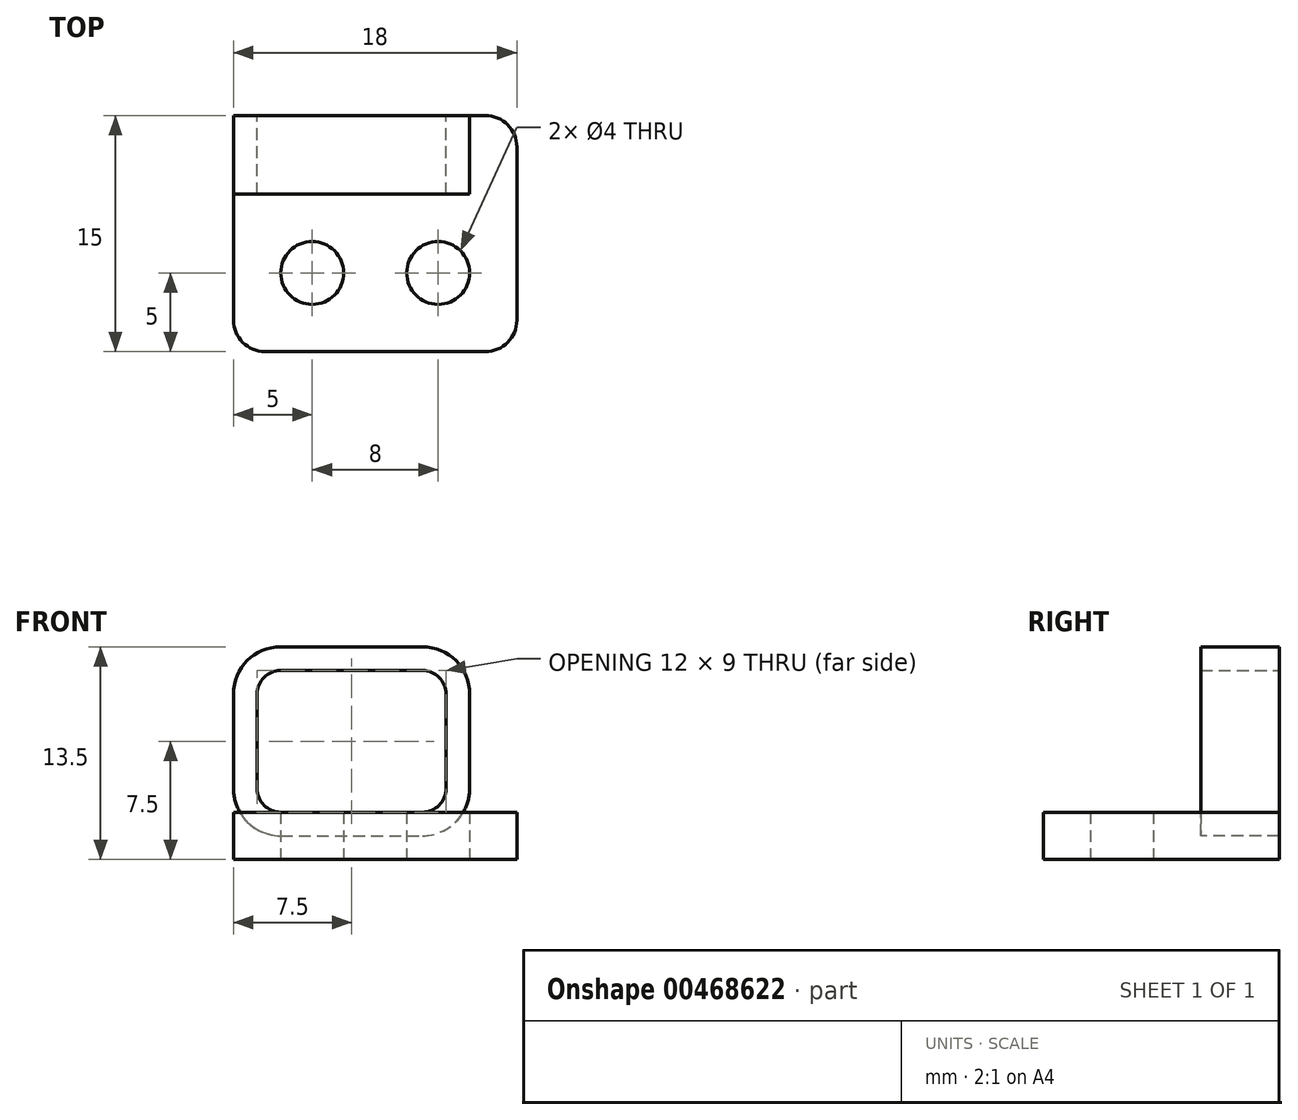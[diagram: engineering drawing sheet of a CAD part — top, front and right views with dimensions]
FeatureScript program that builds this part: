
annotation { "Feature Type Name" : "Feature", "Feature Type Description" : "" }
export const myFeature = defineFeature(function(context is Context, id is Id, definition is map)
    precondition{}
    {
        {
            assignVariable(context, id + "F0", {"name" : "finger_thickness", "anyValue" : 12 * mm});
        }
        {
            assignVariable(context, id + "F1", {"name" : "wall_thickness", "anyValue" : 1.5 * mm});
        }
        {
            var Q0;
            Q0=qCreatedBy(makeId("Top.planeOp"),FACE);
            var sketch = newSketch(context, id + "F2", { "sketchPlane" : qUnion([Q0])});
            skLineSegment(sketch, "E0.bottom", {"start": v(0, 0) * mm, "end": v(15, 0) * mm});
            skLineSegment(sketch, "E0.top", {"start": v(0, -5) * mm, "end": v(15, -5) * mm});
            skLineSegment(sketch, "E0.left", {"start": v(0, 0) * mm, "end": v(0, -5) * mm});
            skLineSegment(sketch, "E0.right", {"start": v(15, 0) * mm, "end": v(15, -5) * mm});
            skLineSegment(sketch, "E1", {"start": v(0, -5) * mm, "end": v(0, -15) * mm});
            skLineSegment(sketch, "E2", {"start": v(0, -15) * mm, "end": v(18, -15) * mm});
            skLineSegment(sketch, "E3", {"start": v(18, -15) * mm, "end": v(18, 0) * mm});
            skPoint(sketch, "E4.centerSnap1", {"position": v(9, -15) * mm});
            skLineSegment(sketch, "E5", {"start": v(15, 0) * mm, "end": v(18, 0) * mm});
            skCircle(sketch, "E6", {"center": v(13, -10) * mm, "radius": 2 * mm});
            skCircle(sketch, "E7", {"center": v(5, -10) * mm, "radius": 2 * mm});
            skSolve(sketch);
        }
        {
            var Q0;
            Q0=makeQuery(id+"F2.imprint","IMPRINT",FACE,{"disambiguationData":[TD([[makeQuery(id+"F2.imprint","IMPRINT",EDGE,{"derivedFrom":sQuery(id+"F2.wireOp",EDGE,"E0.top")}),-1.0]])]});
            var Q1;
            Q1=makeQuery(id+"F2.imprint","IMPRINT",FACE,{"disambiguationData":[TD([[makeQuery(id+"F2.imprint","IMPRINT",EDGE,{"derivedFrom":sQuery(id+"F2.wireOp",EDGE,"E0.bottom")}),-1.0]])]});
            extrude(context, id + "F3", {"entities" : qUnion([Q0, Q1]), "depth" : getVariable(context, 'wall_thickness'), "offsetDistance" : 25 * mm, "hasSecondDirection" : true, "secondDirectionOppositeDirection" : true, "secondDirectionDepth" : 1.5 * mm});
        }
        {
            var Q0;
            Q0=makeQuery(id+"F2.imprint","IMPRINT",FACE,{"disambiguationData":[TD([[makeQuery(id+"F2.imprint","IMPRINT",EDGE,{"derivedFrom":sQuery(id+"F2.wireOp",EDGE,"E0.bottom")}),-1.0]])]});
            extrude(context, id + "F4", {"entities" : qUnion([Q0]), "depth" : getVariable(context, 'finger_thickness'), "offsetDistance" : 25 * mm});
        }
        {
            var Q0;
            Q0=makeQuery(id+"F4.opExtrude","CAP_EDGE",EDGE,{"disambiguationData":[OSD([sQuery(id+"F2.wireOp",EDGE,"E0.left")])],"isStart":false});
            var Q1;
            Q1=makeQuery(id+"F4.opExtrude","CAP_EDGE",EDGE,{"disambiguationData":[OSD([sQuery(id+"F2.wireOp",EDGE,"E0.right")])],"isStart":false});
            var Q2;
            Q2=makeQuery(id+"F4.opExtrude","CAP_EDGE",EDGE,{"disambiguationData":[OSD([sQuery(id+"F2.wireOp",EDGE,"E0.right")])],"isStart":true});
            var Q3;
            Q3=makeQuery(id+"F4.opExtrude","CAP_EDGE",EDGE,{"disambiguationData":[OSD([sQuery(id+"F2.wireOp",EDGE,"E0.left")])],"isStart":true});
            fillet(context, id + "F5", {"entities" : qUnion([Q0, Q1, Q2, Q3]), "radius" : 3 * mm, "tangentPropagation" : true, "allowEdgeOverflow" : false});
        }
        {
            var Q0;
            Q0=makeQuery(id+"F4.opExtrude","SWEPT_FACE",FACE,{"disambiguationData":[OSD([sQuery(id+"F2.wireOp",EDGE,"E0.top")])]});
            var Q1;
            Q1=makeQuery(id+"F4.opExtrude","SWEPT_FACE",FACE,{"disambiguationData":[OSD([sQuery(id+"F2.wireOp",EDGE,"E0.bottom")])]});
            shell(context, id + "F6", {"entities" : qUnion([Q0, Q1]), "thickness" : getVariable(context, 'wall_thickness')});
        }
        {
            var Q0;
            Q0=makeQuery(id+"F3.opExtrude","SWEPT_EDGE",EDGE,{"disambiguationData":[OSD([sQuery(id+"F2.wireOp",EDGE,"E1"),sQuery(id+"F2.wireOp",EDGE,"E2")])]});
            var Q1;
            Q1=makeQuery(id+"F3.opExtrude","SWEPT_EDGE",EDGE,{"disambiguationData":[OSD([sQuery(id+"F2.wireOp",EDGE,"E2"),sQuery(id+"F2.wireOp",EDGE,"E3")])]});
            var Q2;
            Q2=makeQuery(id+"F3.opExtrude","SWEPT_EDGE",EDGE,{"disambiguationData":[OSD([sQuery(id+"F2.wireOp",EDGE,"E3"),sQuery(id+"F2.wireOp",EDGE,"E5")])]});
            fillet(context, id + "F7", {"entities" : qUnion([Q0, Q1, Q2]), "radius" : 2 * mm, "tangentPropagation" : true, "allowEdgeOverflow" : false});
        }
    });
